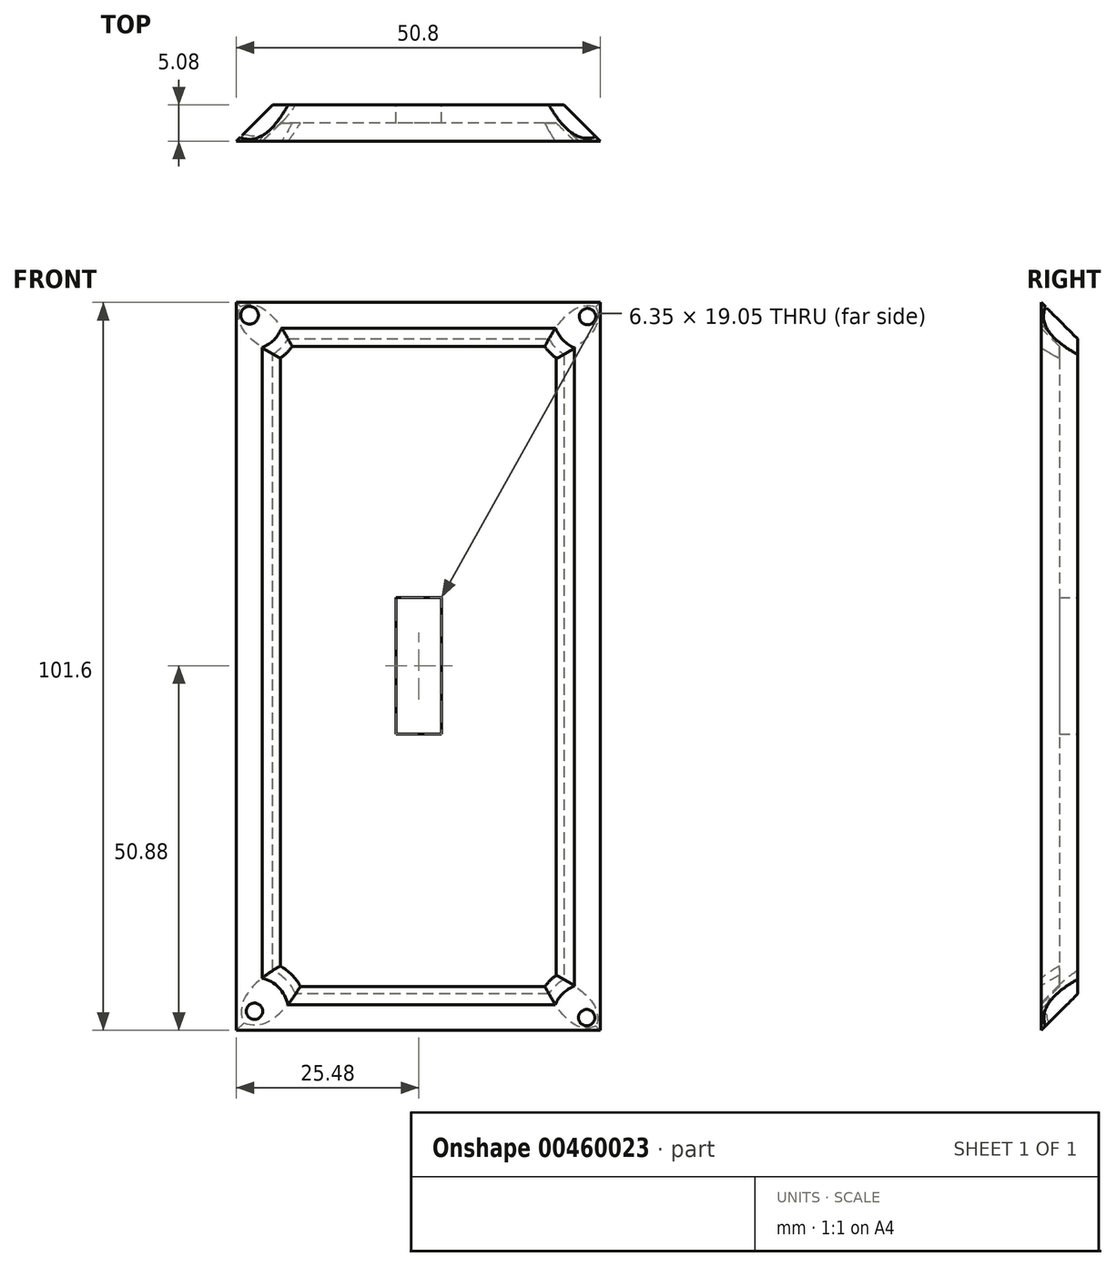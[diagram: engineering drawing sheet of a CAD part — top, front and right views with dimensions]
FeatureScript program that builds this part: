
annotation { "Feature Type Name" : "Feature", "Feature Type Description" : "" }
export const myFeature = defineFeature(function(context is Context, id is Id, definition is map)
    precondition{}
    {
        {
            var Q0;
            Q0=qCreatedBy(makeId("Front.planeOp"),FACE);
            var sketch = newSketch(context, id + "F0", { "sketchPlane" : qUnion([Q0])});
            skLineSegment(sketch, "E0.bottom", {"start": v(25.32, 50.72) * mm, "end": v(-25.48, 50.72) * mm});
            skLineSegment(sketch, "E0.top", {"start": v(25.32, -50.88) * mm, "end": v(-25.48, -50.88) * mm});
            skLineSegment(sketch, "E0.left", {"start": v(25.32, 50.72) * mm, "end": v(25.32, -50.88) * mm});
            skLineSegment(sketch, "E0.right", {"start": v(-25.48, 50.72) * mm, "end": v(-25.48, -50.88) * mm});
            skPoint(sketch, "E0.middle", {"position": v(-0.08, -0.08) * mm});
            skCircle(sketch, "E1", {"center": v(-23.63, 48.94) * mm, "radius": 1.24 * mm});
            skCircle(sketch, "E2", {"center": v(23.53, 48.75) * mm, "radius": 1.14 * mm});
            skCircle(sketch, "E3", {"center": v(23.42, -49.1) * mm, "radius": 1.14 * mm});
            skCircle(sketch, "E4", {"center": v(-22.94, -48.2) * mm, "radius": 1.14 * mm});
            skSolve(sketch);
        }
        {
            var Q0;
            Q0=makeQuery(id+"F0.imprint","IMPRINT",FACE,{"disambiguationData":[TD([[makeQuery(id+"F0.imprint","IMPRINT",EDGE,{"derivedFrom":sQuery(id+"F0.wireOp",EDGE,"E0.bottom")}),1.0]])]});
            extrude(context, id + "F1", {"entities" : qUnion([Q0]), "depth" : 5.08 * mm});
        }
        {
            var Q0;
            Q0=makeQuery(id+"F1.opExtrude","CAP_EDGE",EDGE,{"disambiguationData":[OSD([sQuery(id+"F0.wireOp",EDGE,"E0.left")])],"isStart":true});
            var Q1;
            Q1=makeQuery(id+"F1.opExtrude","CAP_EDGE",EDGE,{"disambiguationData":[OSD([sQuery(id+"F0.wireOp",EDGE,"E0.bottom")])],"isStart":true});
            var Q2;
            Q2=makeQuery(id+"F1.opExtrude","CAP_EDGE",EDGE,{"disambiguationData":[OSD([sQuery(id+"F0.wireOp",EDGE,"E0.right")])],"isStart":true});
            var Q3;
            Q3=makeQuery(id+"F1.opExtrude","CAP_EDGE",EDGE,{"disambiguationData":[OSD([sQuery(id+"F0.wireOp",EDGE,"E0.top")])],"isStart":true});
            var Q4;
            Q4=makeQuery(id+"F1.opExtrude","CAP_EDGE",EDGE,{"disambiguationData":[OSD([sQuery(id+"F0.wireOp",EDGE,"E1")])],"isStart":true});
            var Q5;
            Q5=makeQuery(id+"F1.opExtrude","CAP_EDGE",EDGE,{"disambiguationData":[OSD([sQuery(id+"F0.wireOp",EDGE,"E2")])],"isStart":true});
            var Q6;
            Q6=makeQuery(id+"F1.opExtrude","CAP_FACE",FACE,{"disambiguationData":[OSD([sQuery(id+"F0.wireOp",EDGE,"E0.bottom"),sQuery(id+"F0.wireOp",EDGE,"E0.top"),sQuery(id+"F0.wireOp",EDGE,"E0.left"),sQuery(id+"F0.wireOp",EDGE,"E0.right"),sQuery(id+"F0.wireOp",EDGE,"E1"),sQuery(id+"F0.wireOp",EDGE,"E2"),sQuery(id+"F0.wireOp",EDGE,"E3"),sQuery(id+"F0.wireOp",EDGE,"E4")])],"isStart":true});
            chamfer(context, id + "F2", {"entities" : qUnion([Q0, Q1, Q2, Q3, Q4, Q5, Q6]), "width" : 5.08 * mm, "tangentPropagation" : true});
        }
        {
            var Q0;
            Q0=makeQuery(id+"F1.opExtrude","CAP_FACE",FACE,{"disambiguationData":[OSD([sQuery(id+"F0.wireOp",EDGE,"E0.bottom"),sQuery(id+"F0.wireOp",EDGE,"E0.top"),sQuery(id+"F0.wireOp",EDGE,"E0.left"),sQuery(id+"F0.wireOp",EDGE,"E0.right"),sQuery(id+"F0.wireOp",EDGE,"E1"),sQuery(id+"F0.wireOp",EDGE,"E2"),sQuery(id+"F0.wireOp",EDGE,"E3"),sQuery(id+"F0.wireOp",EDGE,"E4")])],"isStart":false});
            shell(context, id + "F3", {"entities" : qUnion([Q0]), "thickness" : 2.54 * mm});
        }
        {
            var Q0;
            Q0=makeQuery(id+"F1.opExtrude","CAP_FACE",FACE,{"disambiguationData":[OSD([sQuery(id+"F0.wireOp",EDGE,"E0.bottom"),sQuery(id+"F0.wireOp",EDGE,"E0.top"),sQuery(id+"F0.wireOp",EDGE,"E0.left"),sQuery(id+"F0.wireOp",EDGE,"E0.right"),sQuery(id+"F0.wireOp",EDGE,"E1"),sQuery(id+"F0.wireOp",EDGE,"E2"),sQuery(id+"F0.wireOp",EDGE,"E3"),sQuery(id+"F0.wireOp",EDGE,"E4")])],"isStart":true});
            var sketch = newSketch(context, id + "F4", { "sketchPlane" : qUnion([Q0])});
            skLineSegment(sketch, "E5.bottom", {"start": v(3.18, -9.53) * mm, "end": v(-3.18, -9.53) * mm});
            skLineSegment(sketch, "E5.top", {"start": v(3.17, 9.53) * mm, "end": v(-3.18, 9.53) * mm});
            skLineSegment(sketch, "E5.left", {"start": v(3.18, -9.53) * mm, "end": v(3.17, 9.53) * mm});
            skLineSegment(sketch, "E5.right", {"start": v(-3.18, -9.53) * mm, "end": v(-3.18, 9.53) * mm});
            skPoint(sketch, "E5.middle", {"position": v(0, 0) * mm});
            skSolve(sketch);
        }
        {
            var Q0;
            Q0=makeQuery(id+"F4.imprint","IMPRINT",FACE,{"disambiguationData":[TD([[makeQuery(id+"F4.imprint","IMPRINT",EDGE,{"derivedFrom":sQuery(id+"F4.wireOp",EDGE,"E5.bottom")}),-1.0]])]});
            extrude(context, id + "F5", {"entities" : qUnion([Q0]), "operationType" : NewBodyOperationType.REMOVE, "oppositeDirection" : true, "depth" : 25.4 * mm});
        }
    });
